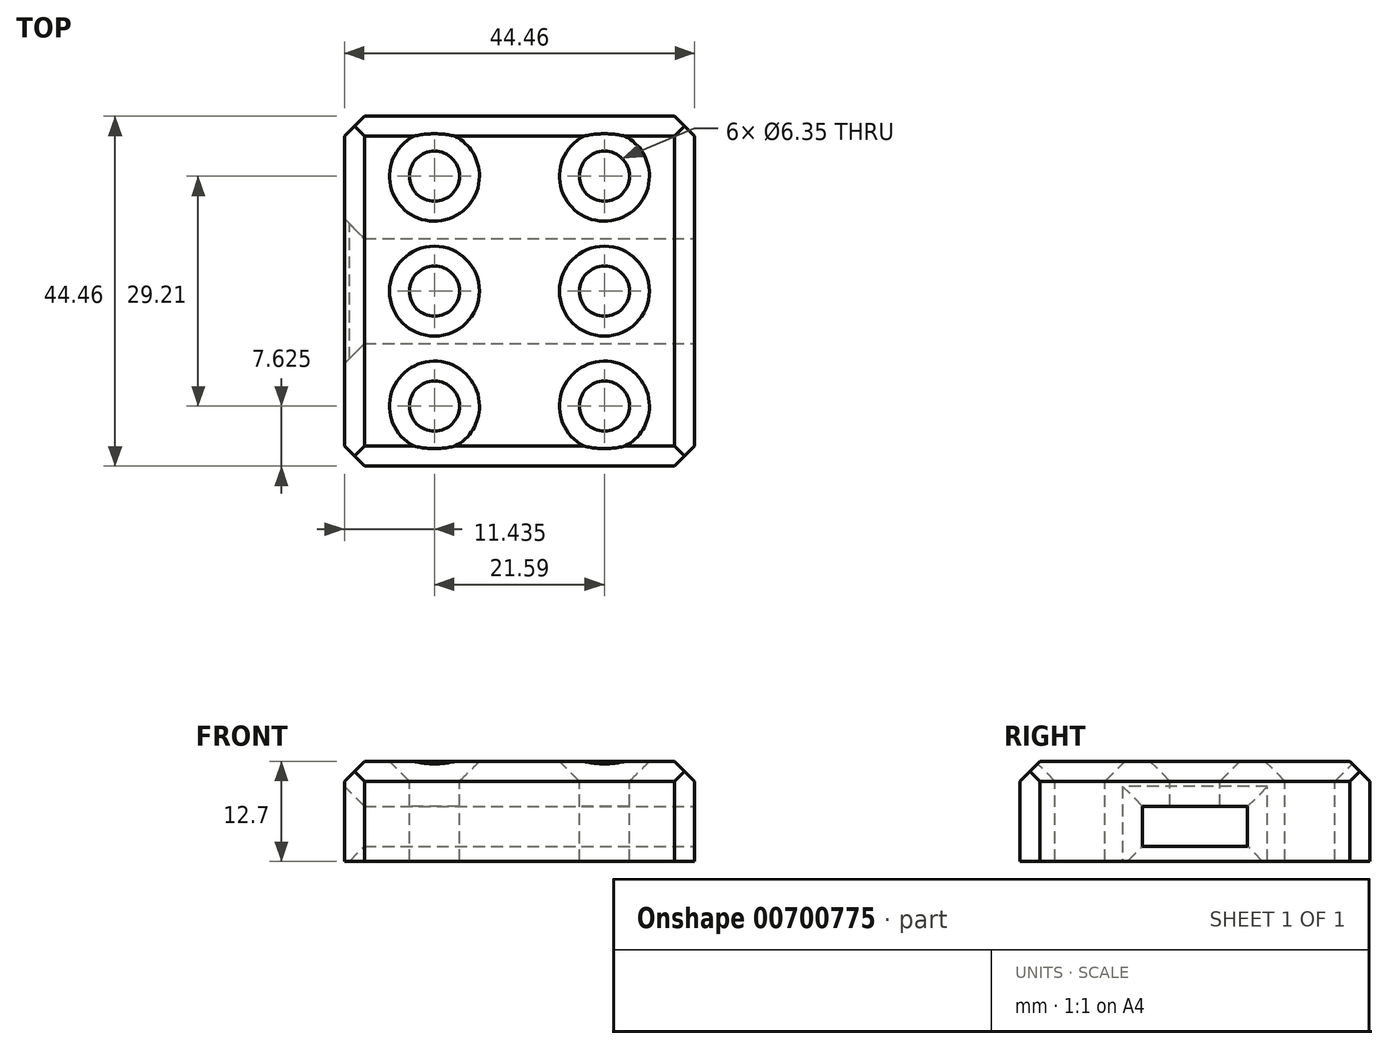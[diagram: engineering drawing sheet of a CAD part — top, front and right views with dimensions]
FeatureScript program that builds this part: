
annotation { "Feature Type Name" : "Feature", "Feature Type Description" : "" }
export const myFeature = defineFeature(function(context is Context, id is Id, definition is map)
    precondition{}
    {
        {
            var Q0;
            Q0=qCreatedBy(makeId("Top.planeOp"),FACE);
            var sketch = newSketch(context, id + "F0", { "sketchPlane" : qUnion([Q0])});
            skLineSegment(sketch, "E0.bottom", {"start": v(22.22, 22.23) * mm, "end": v(-22.23, 22.23) * mm});
            skLineSegment(sketch, "E0.top", {"start": v(22.22, -22.23) * mm, "end": v(-22.23, -22.23) * mm});
            skLineSegment(sketch, "E0.left", {"start": v(22.22, 22.23) * mm, "end": v(22.22, -22.23) * mm});
            skLineSegment(sketch, "E0.right", {"start": v(-22.23, 22.23) * mm, "end": v(-22.23, -22.23) * mm});
            skPoint(sketch, "E0.middle", {"position": v(0, 0) * mm});
            skSolve(sketch);
        }
        {
            var Q0;
            Q0=makeQuery(id+"F0.imprint","IMPRINT",FACE,{"disambiguationData":[TD([[makeQuery(id+"F0.imprint","IMPRINT",EDGE,{"derivedFrom":sQuery(id+"F0.wireOp",EDGE,"E0.bottom")}),1.0]])]});
            extrude(context, id + "F1", {"entities" : qUnion([Q0]), "depth" : 12.7 * mm, "offsetDistance" : 25.4 * mm});
        }
        {
            var Q0;
            Q0=makeQuery(id+"F1.opExtrude","SWEPT_FACE",FACE,{"disambiguationData":[OSD([sQuery(id+"F0.wireOp",EDGE,"E0.left")])]});
            var sketch = newSketch(context, id + "F2", { "sketchPlane" : qUnion([Q0])});
            skLineSegment(sketch, "E1.bottom", {"start": v(6.67, 1.9) * mm, "end": v(-6.67, 1.9) * mm});
            skLineSegment(sketch, "E1.top", {"start": v(6.67, 6.99) * mm, "end": v(-6.67, 6.99) * mm});
            skLineSegment(sketch, "E1.left", {"start": v(6.67, 1.9) * mm, "end": v(6.67, 6.99) * mm});
            skLineSegment(sketch, "E1.right", {"start": v(-6.67, 1.9) * mm, "end": v(-6.67, 6.99) * mm});
            skPoint(sketch, "E1.middle", {"position": v(0, 4.45) * mm});
            skSolve(sketch);
        }
        {
            var Q0;
            Q0=makeQuery(id+"F2.imprint","IMPRINT",FACE,{"disambiguationData":[TD([[makeQuery(id+"F2.imprint","IMPRINT",EDGE,{"derivedFrom":sQuery(id+"F2.wireOp",EDGE,"E1.bottom")}),-1.0]])]});
            extrude(context, id + "F3", {"entities" : qUnion([Q0]), "operationType" : NewBodyOperationType.REMOVE, "oppositeDirection" : true, "depth" : 76.2 * mm, "offsetDistance" : 25.4 * mm});
        }
        {
            var Q0;
            Q0=makeQuery(id+"F1.opExtrude","CAP_FACE",FACE,{"disambiguationData":[OSD([sQuery(id+"F0.wireOp",EDGE,"E0.bottom"),sQuery(id+"F0.wireOp",EDGE,"E0.top"),sQuery(id+"F0.wireOp",EDGE,"E0.left"),sQuery(id+"F0.wireOp",EDGE,"E0.right")])],"isStart":false});
            var sketch = newSketch(context, id + "F4", { "sketchPlane" : qUnion([Q0])});
            skCircle(sketch, "E2", {"center": v(10.8, 14.6) * mm, "radius": 3.18 * mm});
            skCircle(sketch, "E3.MirrorC", {"center": v(-10.8, 14.6) * mm, "radius": 3.18 * mm});
            skCircle(sketch, "E4.MirrorC", {"center": v(-10.8, -14.6) * mm, "radius": 3.18 * mm});
            skCircle(sketch, "E5.MirrorC", {"center": v(10.8, -14.6) * mm, "radius": 3.18 * mm});
            skCircle(sketch, "E6", {"center": v(-10.8, 0) * mm, "radius": 3.18 * mm});
            skCircle(sketch, "E7.MirrorC", {"center": v(10.8, 0) * mm, "radius": 3.18 * mm});
            skSolve(sketch);
        }
        {
            var Q0;
            Q0 = qSketchRegion(id + "F4", true);
            extrude(context, id + "F5", {"entities" : qUnion([Q0]), "operationType" : NewBodyOperationType.REMOVE, "oppositeDirection" : true, "depth" : 25.4 * mm, "offsetDistance" : 25.4 * mm});
        }
        {
            var Q0;
            Q0=makeQuery(id+"F1.opExtrude","CAP_FACE",FACE,{"disambiguationData":[OSD([sQuery(id+"F0.wireOp",EDGE,"E0.bottom"),sQuery(id+"F0.wireOp",EDGE,"E0.top"),sQuery(id+"F0.wireOp",EDGE,"E0.left"),sQuery(id+"F0.wireOp",EDGE,"E0.right")])],"isStart":false});
            chamfer(context, id + "F6", {"entities" : qUnion([Q0]), "width" : 2.54 * mm, "tangentPropagation" : true});
        }
        {
            var Q0;
            Q0=makeQuery(id+"F3.boolean.opBoolean","COPY",EDGE,{"derivedFrom":makeQuery(id+"F3.opExtrude","CAP_EDGE",EDGE,{"disambiguationData":[OSD([sQuery(id+"F2.wireOp",EDGE,"E1.left")])],"isStart":true})});
            var Q1;
            Q1=makeQuery(id+"F3.boolean.opBoolean","COPY",EDGE,{"derivedFrom":makeQuery(id+"F3.opExtrude","CAP_EDGE",EDGE,{"disambiguationData":[OSD([sQuery(id+"F2.wireOp",EDGE,"E1.bottom")])],"isStart":true})});
            var Q2;
            Q2=makeQuery(id+"F3.boolean.opBoolean","COPY",EDGE,{"derivedFrom":makeQuery(id+"F3.opExtrude","CAP_EDGE",EDGE,{"disambiguationData":[OSD([sQuery(id+"F2.wireOp",EDGE,"E1.top")])],"isStart":true})});
            var Q3;
            Q3=makeQuery(id+"F3.boolean.opBoolean","COPY",EDGE,{"derivedFrom":makeQuery(id+"F3.opExtrude","CAP_EDGE",EDGE,{"disambiguationData":[OSD([sQuery(id+"F2.wireOp",EDGE,"E1.right")])],"isStart":true})});
            var Q4;
            Q4=makeQuery(id+"F3.boolean.opBoolean","INTERSECT",EDGE,{"derivedFrom":[makeQuery(id+"F1.opExtrude","SWEPT_FACE",FACE,{"disambiguationData":[OSD([sQuery(id+"F0.wireOp",EDGE,"E0.right")])]}),makeQuery(id+"F3.opExtrude","SWEPT_FACE",FACE,{"disambiguationData":[OSD([sQuery(id+"F2.wireOp",EDGE,"E1.top")])]})]});
            var Q5;
            Q5=makeQuery(id+"F3.boolean.opBoolean","INTERSECT",EDGE,{"derivedFrom":[makeQuery(id+"F1.opExtrude","SWEPT_FACE",FACE,{"disambiguationData":[OSD([sQuery(id+"F0.wireOp",EDGE,"E0.right")])]}),makeQuery(id+"F3.opExtrude","SWEPT_FACE",FACE,{"disambiguationData":[OSD([sQuery(id+"F2.wireOp",EDGE,"E1.left")])]})]});
            var Q6;
            Q6=makeQuery(id+"F3.boolean.opBoolean","INTERSECT",EDGE,{"derivedFrom":[makeQuery(id+"F1.opExtrude","SWEPT_FACE",FACE,{"disambiguationData":[OSD([sQuery(id+"F0.wireOp",EDGE,"E0.right")])]}),makeQuery(id+"F3.opExtrude","SWEPT_FACE",FACE,{"disambiguationData":[OSD([sQuery(id+"F2.wireOp",EDGE,"E1.bottom")])]})]});
            var Q7;
            Q7=makeQuery(id+"F3.boolean.opBoolean","INTERSECT",EDGE,{"derivedFrom":[makeQuery(id+"F1.opExtrude","SWEPT_FACE",FACE,{"disambiguationData":[OSD([sQuery(id+"F0.wireOp",EDGE,"E0.right")])]}),makeQuery(id+"F3.opExtrude","SWEPT_FACE",FACE,{"disambiguationData":[OSD([sQuery(id+"F2.wireOp",EDGE,"E1.right")])]})]});
            var Q8;
            Q8=makeQuery(id+"F1.opExtrude","SWEPT_EDGE",EDGE,{"disambiguationData":[OSD([sQuery(id+"F0.wireOp",EDGE,"E0.top"),sQuery(id+"F0.wireOp",EDGE,"E0.right")])]});
            var Q9;
            Q9=makeQuery(id+"F1.opExtrude","SWEPT_EDGE",EDGE,{"disambiguationData":[OSD([sQuery(id+"F0.wireOp",EDGE,"E0.top"),sQuery(id+"F0.wireOp",EDGE,"E0.left")])]});
            var Q10;
            Q10=makeQuery(id+"F1.opExtrude","SWEPT_EDGE",EDGE,{"disambiguationData":[OSD([sQuery(id+"F0.wireOp",EDGE,"E0.bottom"),sQuery(id+"F0.wireOp",EDGE,"E0.left")])]});
            var Q11;
            Q11=makeQuery(id+"F1.opExtrude","SWEPT_EDGE",EDGE,{"disambiguationData":[OSD([sQuery(id+"F0.wireOp",EDGE,"E0.bottom"),sQuery(id+"F0.wireOp",EDGE,"E0.right")])]});
            chamfer(context, id + "F7", {"entities" : qUnion([Q0, Q1, Q2, Q3, Q4, Q5, Q6, Q7, Q8, Q9, Q10, Q11]), "width" : 2.54 * mm, "tangentPropagation" : true});
        }
        {
            var Q0;
            Q0=makeQuery(id+"F1.opExtrude","CAP_FACE",FACE,{"disambiguationData":[OSD([sQuery(id+"F0.wireOp",EDGE,"E0.bottom"),sQuery(id+"F0.wireOp",EDGE,"E0.top"),sQuery(id+"F0.wireOp",EDGE,"E0.left"),sQuery(id+"F0.wireOp",EDGE,"E0.right")])],"isStart":true});
            var sketch = newSketch(context, id + "F8", { "sketchPlane" : qUnion([Q0])});
            skCircle(sketch, "E8", {"center": v(10.8, 0) * mm, "radius": 3.18 * mm});
            skCircle(sketch, "E9", {"center": v(-10.8, 0) * mm, "radius": 3.18 * mm});
            skSolve(sketch);
        }
        {
            var Q0;
            Q0 = qSketchRegion(id + "F8", true);
            var Q1;
            Q1=makeQuery(id+"F3.boolean.opBoolean","COPY",FACE,{"derivedFrom":makeQuery(id+"F3.opExtrude","SWEPT_FACE",FACE,{"disambiguationData":[OSD([sQuery(id+"F2.wireOp",EDGE,"E1.bottom")])]})});
            extrude(context, id + "F9", {"entities" : qUnion([Q0]), "operationType" : NewBodyOperationType.ADD, "endBound" : BoundingType.UP_TO_SURFACE, "oppositeDirection" : true, "depth" : 25.4 * mm, "endBoundEntityFace" : qUnion([Q1]), "offsetDistance" : 25.4 * mm});
        }
    });
